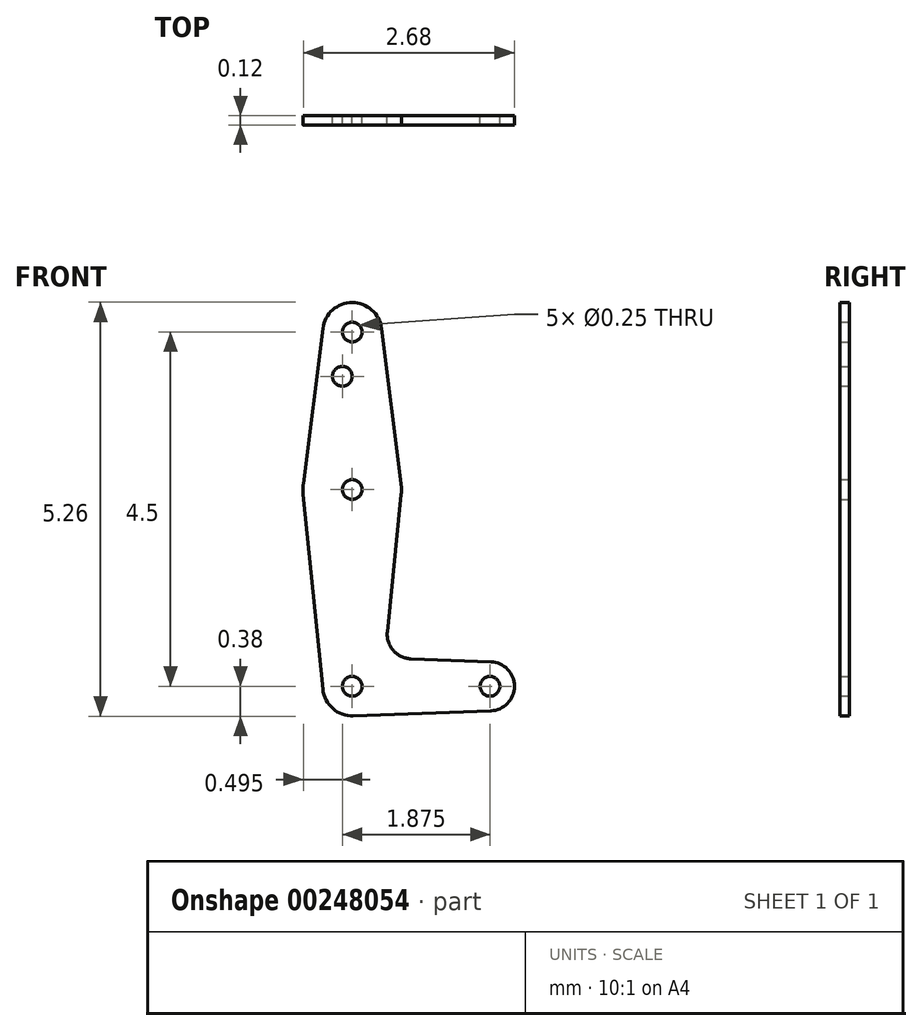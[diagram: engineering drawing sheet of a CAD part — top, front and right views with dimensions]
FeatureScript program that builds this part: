
annotation { "Feature Type Name" : "Feature", "Feature Type Description" : "" }
export const myFeature = defineFeature(function(context is Context, id is Id, definition is map)
    precondition{}
    {
        {
            var Q0;
            Q0=qCreatedBy(makeId("Front.planeOp"),FACE);
            var sketch = newSketch(context, id + "F0", { "sketchPlane" : qUnion([Q0])});
            skLineSegment(sketch, "E0", {"start": v(0, 0) * mm, "end": v(1.75, 0) * mm, "construction": true});
            skLineSegment(sketch, "E1", {"start": v(0, 0) * mm, "end": v(0, 4.5) * mm, "construction": true});
            skCircle(sketch, "E2", {"center": v(0, 4.5) * mm, "radius": 0.38 * mm});
            skCircle(sketch, "E3", {"center": v(0, 2.5) * mm, "radius": 0.62 * mm});
            skCircle(sketch, "E4", {"center": v(0, 0) * mm, "radius": 0.38 * mm});
            skCircle(sketch, "E5", {"center": v(1.75, 0) * mm, "radius": 0.31 * mm});
            skLineSegment(sketch, "E6", {"start": v(1.76, -0.31) * mm, "end": v(0.01, -0.37) * mm});
            skLineSegment(sketch, "E7", {"start": v(-0.37, -0.04) * mm, "end": v(-0.62, 2.44) * mm});
            skLineSegment(sketch, "E8", {"start": v(-0.62, 2.58) * mm, "end": v(-0.37, 4.55) * mm});
            skLineSegment(sketch, "E9", {"start": v(0.37, 4.55) * mm, "end": v(0.62, 2.58) * mm});
            skLineSegment(sketch, "E10", {"start": v(0.62, 2.44) * mm, "end": v(0.45, 0.7) * mm});
            skLineSegment(sketch, "E11", {"start": v(0.75, 0.35) * mm, "end": v(1.76, 0.31) * mm});
            skCircle(sketch, "E12", {"center": v(0, 4.5) * mm, "radius": 0.12 * mm});
            skCircle(sketch, "E13", {"center": v(-0.12, 3.94) * mm, "radius": 0.12 * mm});
            skCircle(sketch, "E14", {"center": v(0, 2.5) * mm, "radius": 0.12 * mm});
            skCircle(sketch, "E15", {"center": v(0, 0) * mm, "radius": 0.12 * mm});
            skCircle(sketch, "E16", {"center": v(1.75, 0) * mm, "radius": 0.12 * mm});
            skArc(sketch, "E17.filletArc", {"start": v(0.45, 0.7) * mm, "mid": v(0.52, 0.46) * mm, "end": v(0.75, 0.35) * mm});
            skSolve(sketch);
        }
        {
            var Q0;
            Q0 = qSketchRegion(id + "F0", true);
            extrude(context, id + "F1", {"entities" : qUnion([Q0]), "depth" : 0.12 * mm});
        }
    });
